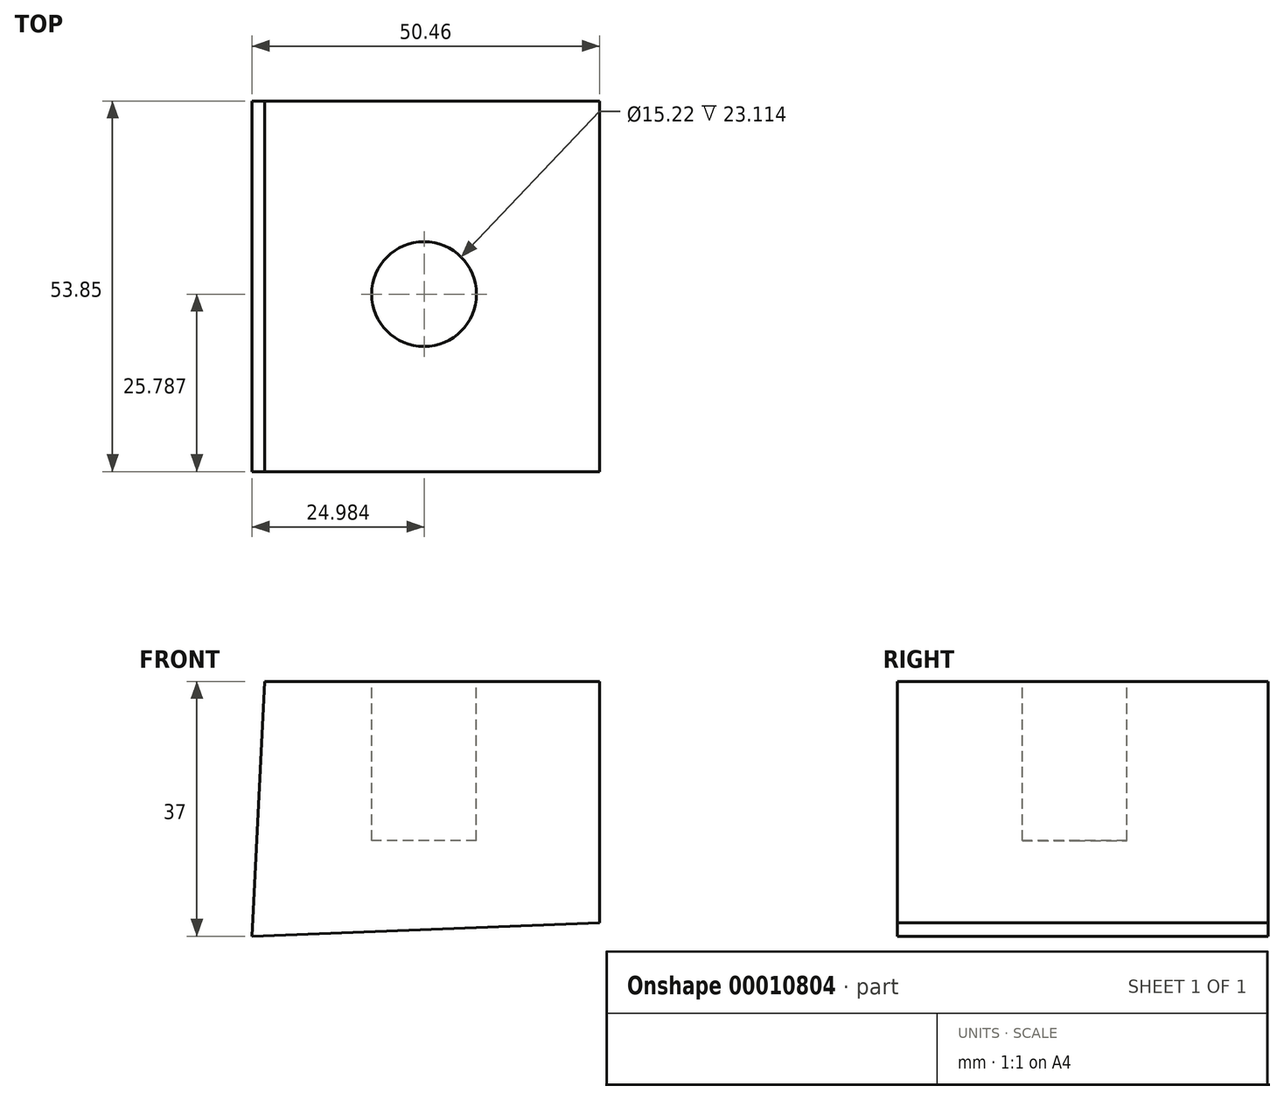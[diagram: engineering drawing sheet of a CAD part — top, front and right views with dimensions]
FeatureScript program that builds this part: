
annotation { "Feature Type Name" : "Feature", "Feature Type Description" : "" }
export const myFeature = defineFeature(function(context is Context, id is Id, definition is map)
    precondition{}
    {
        {
            var Q0;
            Q0=qCreatedBy(makeId("Front.planeOp"),FACE);
            var sketch = newSketch(context, id + "F0", { "sketchPlane" : qUnion([Q0])});
            skLineSegment(sketch, "E0", {"start": v(-22.94, -1.97) * mm, "end": v(-21.09, 35.03) * mm});
            skLineSegment(sketch, "E1", {"start": v(-21.09, 35.03) * mm, "end": v(27.52, 35.03) * mm});
            skLineSegment(sketch, "E2", {"start": v(27.52, 35.03) * mm, "end": v(27.52, 0) * mm});
            skLineSegment(sketch, "E3", {"start": v(27.52, 0) * mm, "end": v(-22.94, -1.97) * mm});
            skSolve(sketch);
        }
        {
            var Q0;
            Q0=makeQuery(id+"F0.imprint","IMPRINT",FACE,{"disambiguationData":[TD([[makeQuery(id+"F0.imprint","IMPRINT",EDGE,{"derivedFrom":sQuery(id+"F0.wireOp",EDGE,"E0")}),-1.0]])]});
            extrude(context, id + "F1", {"entities" : qUnion([Q0]), "depth" : 53.85 * mm, "offsetDistance" : 25.4 * mm});
        }
        {
            var Q0;
            Q0=makeQuery(id+"F1.opExtrude","SWEPT_FACE",FACE,{"disambiguationData":[OSD([sQuery(id+"F0.wireOp",EDGE,"E1")])]});
            var sketch = newSketch(context, id + "F2", { "sketchPlane" : qUnion([Q0])});
            skCircle(sketch, "E4", {"center": v(2.04, -28.06) * mm, "radius": 7.6 * mm});
            skSolve(sketch);
        }
        {
            var Q0;
            Q0=makeQuery(id+"F2.imprint","IMPRINT",FACE,{"disambiguationData":[TD([[makeQuery(id+"F2.imprint","IMPRINT",EDGE,{"derivedFrom":sQuery(id+"F2.wireOp",EDGE,"E4")}),1.0]])]});
            extrude(context, id + "F3", {"entities" : qUnion([Q0]), "operationType" : NewBodyOperationType.REMOVE, "oppositeDirection" : true, "depth" : 23.1 * mm, "offsetDistance" : 25.4 * mm});
        }
    });
